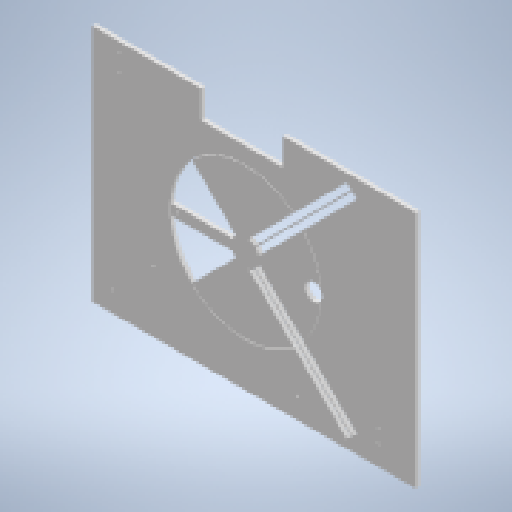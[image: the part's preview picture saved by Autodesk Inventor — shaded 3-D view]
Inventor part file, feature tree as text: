
AUTODESK INVENTOR PART (.ipt)
format: ipt  version: 2023 (Build 270158000, 158)  size: 410,624 bytes
history: native  units: mm
features: extrude x8, sketch x8, other x4, reference x4
ambient origin geometry x8: Origin, YZ Plane, XZ Plane, XY Plane, X Axis, Y Axis, Z Axis, Center Point
bodies: Solid1 (feature_tree)
feature tree (24):
  other  "<userpath>\OneDrive\ClawdDrive\Objet3D\IminaProbe\RoueMDF\Settings.xlsx"
  extrude  "Extrusion1"  Depth=400.0mm
  extrude  "Extrusion2"  TaperAngle=0.0deg  [1 undecoded]
  extrude  "Extrusion3"  Depth=175.0mm
  extrude  "Extrusion4"  Depth=40.0mm
  extrude  "Extrusion5"  Depth=10.0mm
  extrude  "Extrusion6"  Depth=10.0mm
  extrude  "Extrusion7"  Depth=1.0mm
  extrude  "Extrusion8"  Depth=1.0mm
  sketch  "Sketch1"  dims[d0=350.0mm d1=400.0mm]
  sketch  "Sketch2"  dims[d2=6.0mm d3=0.0mm]
  reference  "Reference1"
  sketch  "Sketch3"  dims[d4=175.0mm d5=175.0mm]
  sketch  "Sketch4"  dims[d6=220.0mm d7=40.0mm]
  reference  "Reference5"
  sketch  "Sketch5"  dims[d8=10.0mm d9=10.0mm]
  sketch  "Sketch6"  dims[d10=10.0mm d11=10.0mm]
  sketch  "Sketch7"  dims[d12=1.0mm d13=1.0mm]
  sketch  "Sketch8"  dims[d14=1.0mm d15=1.0mm d16=200.0mm d17=200.0mm d18=222.0mm d19=100.0mm d20=2.25mm d21=2.25mm d22=10.0mm d24=20.0mm d25=0.0mm d26=6.0mm d27=4.0mm d28=4.0mm d29=20.0mm d30=0.0mm d31=3.0mm d32=0.0mm d33=100.0mm d34=6.0mm d35=0.0mm d36=100.0mm d37=25.0mm d38=6.0mm d39=0.0mm d40=40.0mm d41=120.0mm d42=120.0mm d43=6.0mm d44=0.0mm d45=8.0mm d46=8.0mm d47=45.0deg d48=45.0deg d49=10.0mm d50=0.0mm d51=3.0mm d52=15.0mm d53=25.0mm d54=3.0mm d55=40.0mm d56=40.0mm d57=10.0mm d58=0.0mm d59=475.0mm d60=6.0mm d61=0.0mm d62=6.0mm d63=0.0mm]
  reference  "Reference6"
  reference  "Reference7"
  other  "<userpath>\OneDrive\ClawdDrive\Objet3D\IminaProbe\RoueMDF\Assembly1.iam"
  other  "Assembly1.iam"
  other  "Wheel1:1"
note: 1 required parameter value undecoded (feature->parameter linkage not recoverable at this tier; creation-order binding heuristic only, values carry confidence <= 0.55)
